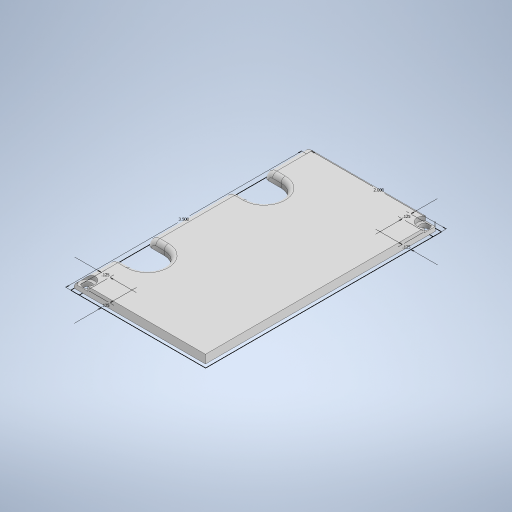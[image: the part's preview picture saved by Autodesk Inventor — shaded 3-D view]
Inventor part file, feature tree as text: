
AUTODESK INVENTOR PART (.ipt)
format: ipt  version: 2024.1 (Build 281209000, 209)  size: 338,944 bytes
history: native  units: in
note: dims shown in document units (in); Inventor stores cm internally (conversion verified against a paired STEP export)
features: extrude x2, fillet x2, hole x1, sketch x1
ambient origin geometry x8: Origin, YZ Plane, XZ Plane, XY Plane, X Axis, Y Axis, Z Axis, Center Point
bodies: Solid1 (feature_tree)
feature tree (6):
  extrude  "Extrusion1"  Depth=0.0625in
  hole  "Hole2"  [1 undecoded]
  fillet  "Fillet1"  Radius=0.125in
  extrude  "Extrusion2"  Depth=0.125in
  fillet  "Fillet2"  Radius=0.125in
  sketch  "Sketch3"  dims[d0=2.0in d1=3.5in d2=0.125in d3=0.125in d4=0.125in d5=0.125in d6=0.125in d7=0.0in d15=0.125in d16=0.125in d17=0.125in d18=0.125in d19=0.129in d20=0.75in d21=0.219in d22=0.0625in d23=0.5635in d24=0.25in d25=0.0in d26=0.125in d27=0.05in d28=0.05in d29=0.05in d30=0.888in d31=0.888in d32=0.25in d33=0.4in d36=1.0in d37=0.0in d40=0.5in d41=0.5in d43=0.0625in]
note: 1 required parameter value undecoded (feature->parameter linkage not recoverable at this tier; creation-order binding heuristic only, values carry confidence <= 0.55)
